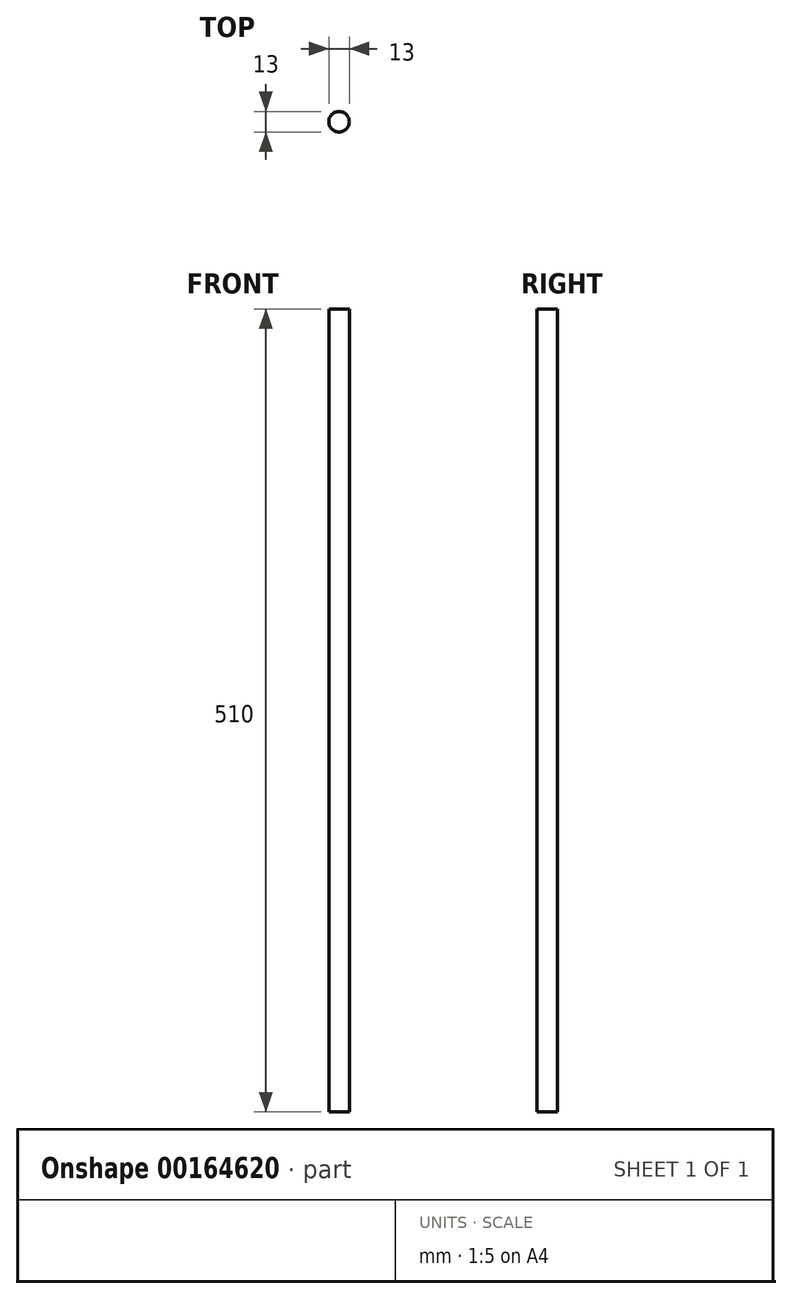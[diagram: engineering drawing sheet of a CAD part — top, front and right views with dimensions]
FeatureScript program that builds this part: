
annotation { "Feature Type Name" : "Feature", "Feature Type Description" : "" }
export const myFeature = defineFeature(function(context is Context, id is Id, definition is map)
    precondition{}
    {
        {
            var Q0;
            Q0=qCreatedBy(makeId("Top.planeOp"),FACE);
            var sketch = newSketch(context, id + "F0", { "sketchPlane" : qUnion([Q0])});
            skCircle(sketch, "E0", {"center": v(0, 0) * mm, "radius": 6.5 * mm});
            skSolve(sketch);
        }
        {
            var Q0;
            Q0=qSketchRegion(id+"F0",true);
            extrude(context, id + "F1", {"entities" : qUnion([Q0]), "endBound" : BoundingType.SYMMETRIC, "depth" : 510 * mm});
        }
    });
